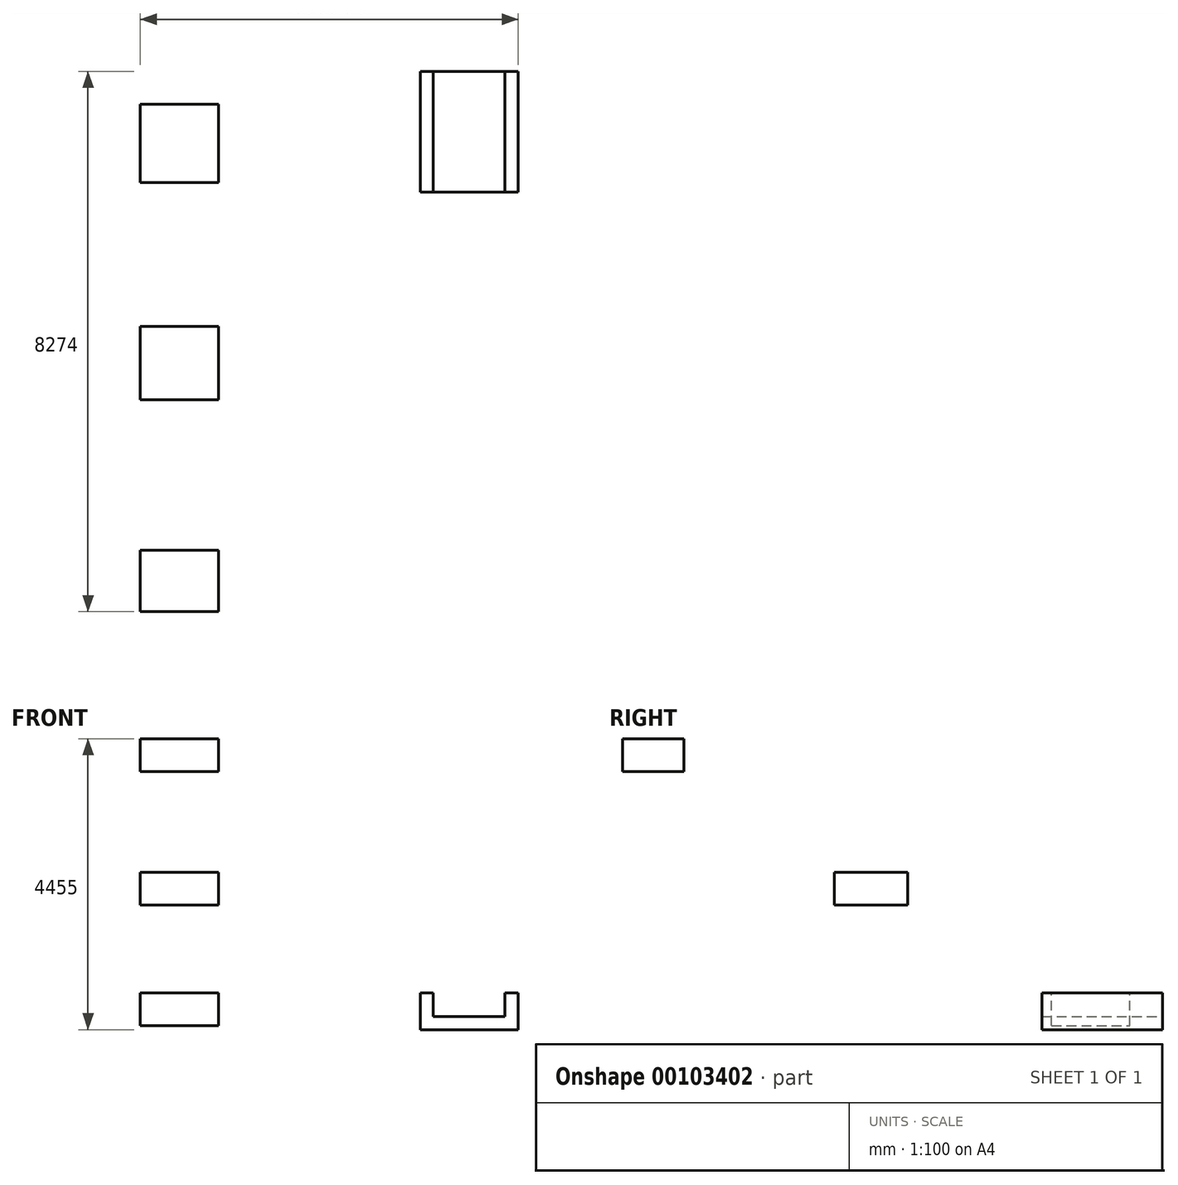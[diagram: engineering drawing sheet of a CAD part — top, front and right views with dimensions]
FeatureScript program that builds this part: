
annotation { "Feature Type Name" : "Feature", "Feature Type Description" : "" }
export const myFeature = defineFeature(function(context is Context, id is Id, definition is map)
    precondition{}
    {
        {
            var Q0;
            Q0=qCreatedBy(makeId("Top.planeOp"),FACE);
            cPlane(context, id + "F0", {"entities" : qUnion([Q0]), "cplaneType" : CPlaneType.OFFSET, "offset" : 5663 * mm, "width" : 150 * mm, "height" : 150 * mm});
        }
        {
            var Q0;
            Q0=qCreatedBy(makeId("Top.planeOp"),FACE);
            cPlane(context, id + "F1", {"entities" : qUnion([Q0]), "cplaneType" : CPlaneType.OFFSET, "offset" : 7509 * mm, "width" : 150 * mm, "height" : 150 * mm});
        }
        {
            var Q0;
            Q0=qCreatedBy(makeId("Top.planeOp"),FACE);
            cPlane(context, id + "F2", {"entities" : qUnion([Q0]), "cplaneType" : CPlaneType.OFFSET, "offset" : 9555 * mm, "width" : 150 * mm, "height" : 150 * mm});
        }
        {
            var Q0;
            Q0=qCreatedBy(id+"F0.planeOp",FACE);
            var sketch = newSketch(context, id + "F3", { "sketchPlane" : qUnion([Q0])});
            skLineSegment(sketch, "E0.bottom", {"start": v(-2550, -1700) * mm, "end": v(-1350, -1700) * mm});
            skLineSegment(sketch, "E0.top", {"start": v(-2550, -500) * mm, "end": v(-1350, -500) * mm});
            skLineSegment(sketch, "E0.left", {"start": v(-2550, -1700) * mm, "end": v(-2550, -500) * mm});
            skLineSegment(sketch, "E0.right", {"start": v(-1350, -1700) * mm, "end": v(-1350, -500) * mm});
            skSolve(sketch);
        }
        {
            var Q0;
            Q0 = qSketchRegion(id + "F3", true);
            extrude(context, id + "F4", {"entities" : qUnion([Q0]), "oppositeDirection" : true, "depth" : 500 * mm, "offsetDistance" : 25 * mm});
        }
        {
            var Q0;
            Q0=qCreatedBy(id+"F1.planeOp",FACE);
            var sketch = newSketch(context, id + "F5", { "sketchPlane" : qUnion([Q0])});
            skLineSegment(sketch, "E1.bottom", {"start": v(-2550, -3907) * mm, "end": v(-1350, -3907) * mm});
            skLineSegment(sketch, "E1.top", {"start": v(-2550, -5027) * mm, "end": v(-1350, -5027) * mm});
            skLineSegment(sketch, "E1.left", {"start": v(-2550, -3907) * mm, "end": v(-2550, -5027) * mm});
            skLineSegment(sketch, "E1.right", {"start": v(-1350, -3907) * mm, "end": v(-1350, -5027) * mm});
            skSolve(sketch);
        }
        {
            var Q0;
            Q0 = qSketchRegion(id + "F5", true);
            extrude(context, id + "F6", {"entities" : qUnion([Q0]), "operationType" : NewBodyOperationType.ADD, "oppositeDirection" : true, "depth" : 500 * mm, "offsetDistance" : 25 * mm});
        }
        {
            var Q0;
            Q0=qCreatedBy(id+"F2.planeOp",FACE);
            var sketch = newSketch(context, id + "F7", { "sketchPlane" : qUnion([Q0])});
            skLineSegment(sketch, "E2.bottom", {"start": v(-2550, -7334) * mm, "end": v(-1350, -7334) * mm});
            skLineSegment(sketch, "E2.top", {"start": v(-2550, -8274) * mm, "end": v(-1350, -8274) * mm});
            skLineSegment(sketch, "E2.left", {"start": v(-2550, -7334) * mm, "end": v(-2550, -8274) * mm});
            skLineSegment(sketch, "E2.right", {"start": v(-1350, -7334) * mm, "end": v(-1350, -8274) * mm});
            skSolve(sketch);
        }
        {
            var Q0;
            Q0 = qSketchRegion(id + "F7", true);
            extrude(context, id + "F8", {"entities" : qUnion([Q0]), "operationType" : NewBodyOperationType.ADD, "oppositeDirection" : true, "depth" : 500 * mm, "offsetDistance" : 25 * mm});
        }
        {
            var Q0;
            Q0=qCreatedBy(makeId("Front.planeOp"),FACE);
            var sketch = newSketch(context, id + "F9", { "sketchPlane" : qUnion([Q0])});
            skLineSegment(sketch, "E3", {"start": v(1738.94, 5663) * mm, "end": v(1738.94, 5100) * mm});
            skLineSegment(sketch, "E4", {"start": v(1738.94, 5100) * mm, "end": v(3238.94, 5100) * mm});
            skLineSegment(sketch, "E5", {"start": v(3238.94, 5100) * mm, "end": v(3238.94, 5663) * mm});
            skLineSegment(sketch, "E6", {"start": v(3238.94, 5663) * mm, "end": v(3038.94, 5663) * mm});
            skLineSegment(sketch, "E7", {"start": v(3038.94, 5663) * mm, "end": v(3038.94, 5300) * mm});
            skLineSegment(sketch, "E8", {"start": v(3038.94, 5300) * mm, "end": v(1938.94, 5300) * mm});
            skLineSegment(sketch, "E9", {"start": v(1938.94, 5300) * mm, "end": v(1938.94, 5663) * mm});
            skLineSegment(sketch, "E10", {"start": v(1938.94, 5663) * mm, "end": v(1738.94, 5663) * mm});
            skSolve(sketch);
        }
        {
            var Q0;
            Q0 = qSketchRegion(id + "F9", true);
            extrude(context, id + "F10", {"entities" : qUnion([Q0]), "operationType" : NewBodyOperationType.ADD, "depth" : 1850 * mm, "offsetDistance" : 25 * mm});
        }
    });
